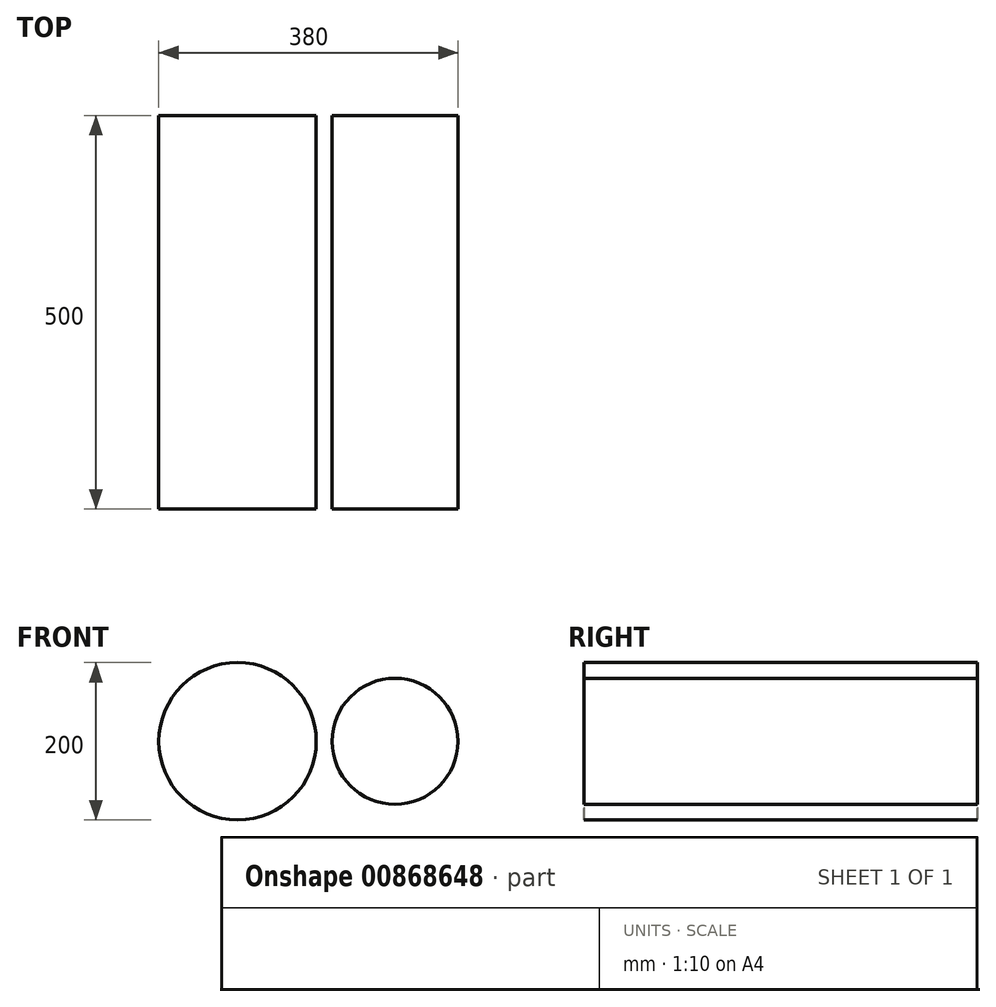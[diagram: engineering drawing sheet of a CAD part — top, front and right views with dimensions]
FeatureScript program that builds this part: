
annotation { "Feature Type Name" : "Feature", "Feature Type Description" : "" }
export const myFeature = defineFeature(function(context is Context, id is Id, definition is map)
    precondition{}
    {
        {
            var Q0;
            Q0=qCreatedBy(makeId("Front.planeOp"),FACE);
            var sketch = newSketch(context, id + "F0", { "sketchPlane" : qUnion([Q0])});
            skCircle(sketch, "E0", {"center": v(0, 0) * mm, "radius": 100 * mm});
            skSolve(sketch);
        }
        {
            var Q0;
            Q0=qCreatedBy(makeId("Front.planeOp"),FACE);
            var sketch = newSketch(context, id + "F1", { "sketchPlane" : qUnion([Q0])});
            skLineSegment(sketch, "E1", {"start": v(0, 0) * mm, "end": v(200, 0) * mm, "construction": true});
            skCircle(sketch, "E2", {"center": v(200, 0) * mm, "radius": 80 * mm});
            skSolve(sketch);
        }
        {
            var Q0;
            Q0=makeQuery(id+"F0.imprint","IMPRINT",FACE,{"disambiguationData":[TD([[makeQuery(id+"F0.imprint","IMPRINT",EDGE,{"derivedFrom":sQuery(id+"F0.wireOp",EDGE,"E0")}),1.0]])]});
            var Q1;
            Q1=makeQuery(id+"F1.imprint","IMPRINT",FACE,{"disambiguationData":[TD([[makeQuery(id+"F1.imprint","IMPRINT",EDGE,{"derivedFrom":sQuery(id+"F1.wireOp",EDGE,"E2")}),1.0]])]});
            var Q2;
            Q2=sQuery(id+"F1.wireOp",EDGE,"E2");
            extrude(context, id + "F2", {"entities" : qUnion([Q0, Q1]), "surfaceEntities" : qUnion([Q2]), "depth" : 500 * mm, "offsetDistance" : 25 * mm});
        }
    });
